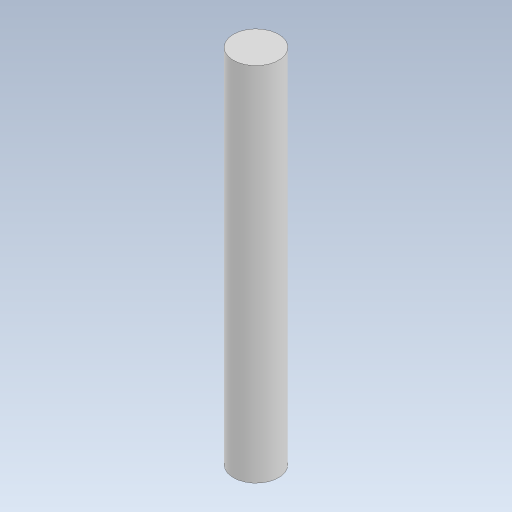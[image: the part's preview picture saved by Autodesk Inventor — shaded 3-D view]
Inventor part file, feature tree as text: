
AUTODESK INVENTOR PART (.ipt)
format: ipt  version: 2023 (Build 270158000, 158)  size: 76,288 bytes
history: native  units: in
note: dims shown in document units (in); Inventor stores cm internally (conversion verified against a paired STEP export)
features: extrude x1, sketch x1
ambient origin geometry x8: Origin, YZ Plane, XZ Plane, XY Plane, X Axis, Y Axis, Z Axis, Center Point
bodies: Solid1 (feature_tree)
feature tree (2):
  extrude  "Extrusion1"  Depth=2.0in TaperAngle=0.0deg
  sketch  "Sketch1"  dims[d0=0.25in d1=2.0in d2=0.0in]
